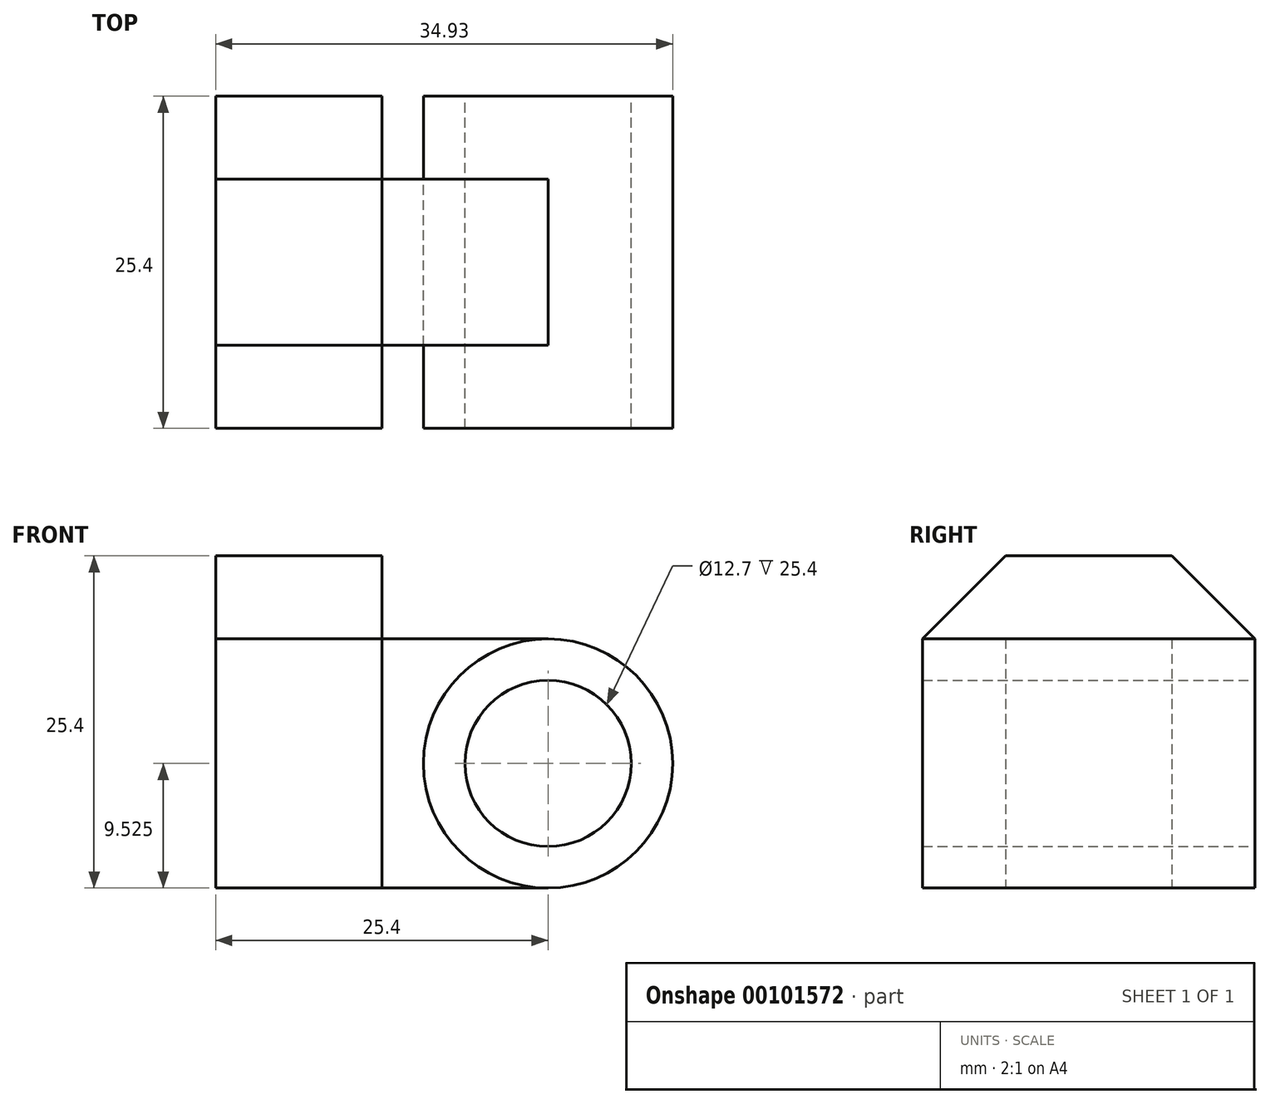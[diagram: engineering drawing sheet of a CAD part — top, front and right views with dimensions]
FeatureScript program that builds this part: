
annotation { "Feature Type Name" : "Feature", "Feature Type Description" : "" }
export const myFeature = defineFeature(function(context is Context, id is Id, definition is map)
    precondition{}
    {
        {
            var Q0;
            Q0=qCreatedBy(makeId("Right.planeOp"),FACE);
            var sketch = newSketch(context, id + "F0", { "sketchPlane" : qUnion([Q0])});
            skLineSegment(sketch, "E0", {"start": v(0, 0) * mm, "end": v(-12.7, 0) * mm});
            skLineSegment(sketch, "E1", {"start": v(12.7, 0) * mm, "end": v(0, 0) * mm});
            skLineSegment(sketch, "E2", {"start": v(-12.7, 0) * mm, "end": v(-12.7, 19.05) * mm});
            skLineSegment(sketch, "E3", {"start": v(-12.7, 19.05) * mm, "end": v(-6.35, 25.4) * mm});
            skLineSegment(sketch, "E4", {"start": v(-6.35, 25.4) * mm, "end": v(6.35, 25.4) * mm});
            skLineSegment(sketch, "E5", {"start": v(6.35, 25.4) * mm, "end": v(12.7, 19.05) * mm});
            skLineSegment(sketch, "E6", {"start": v(12.7, 19.05) * mm, "end": v(12.7, 0) * mm});
            skLineSegment(sketch, "E7", {"start": v(0, 25.4) * mm, "end": v(0, 0) * mm, "construction": true});
            skLineSegment(sketch, "E8", {"start": v(-12.7, 0) * mm, "end": v(-12.7, 25.4) * mm, "construction": true});
            skLineSegment(sketch, "E9", {"start": v(-12.7, 25.4) * mm, "end": v(12.7, 25.4) * mm, "construction": true});
            skLineSegment(sketch, "E10", {"start": v(12.7, 25.4) * mm, "end": v(12.7, 0) * mm, "construction": true});
            skLineSegment(sketch, "E11", {"start": v(12.7, 0) * mm, "end": v(-12.7, 0) * mm, "construction": true});
            skSolve(sketch);
        }
        {
            var Q0;
            Q0 = qSketchRegion(id + "F0", true);
            extrude(context, id + "F1", {"entities" : qUnion([Q0]), "depth" : 12.7 * mm});
        }
        {
            var Q0;
            Q0=qCreatedBy(makeId("Front.planeOp"),FACE);
            var sketch = newSketch(context, id + "F2", { "sketchPlane" : qUnion([Q0])});
            skLineSegment(sketch, "E12", {"start": v(12.7, 0) * mm, "end": v(25.4, 0) * mm});
            skLineSegment(sketch, "E13", {"start": v(25.4, 19.05) * mm, "end": v(12.7, 19.05) * mm});
            skLineSegment(sketch, "E14", {"start": v(12.7, 19.05) * mm, "end": v(12.7, 0) * mm});
            skPoint(sketch, "E15", {"position": v(25.4, 9.53) * mm});
            skCircle(sketch, "E16", {"center": v(25.4, 9.53) * mm, "radius": 6.35 * mm});
            skCircle(sketch, "E17", {"center": v(25.4, 9.53) * mm, "radius": 9.53 * mm});
            skSolve(sketch);
        }
        {
            var Q0;
            Q0=makeQuery(id+"F2.imprint","IMPRINT",FACE,{"disambiguationData":[TD([[makeQuery(id+"F2.imprint","IMPRINT",EDGE,{"derivedFrom":sQuery(id+"F2.wireOp",EDGE,"E16")}),-1.0]])]});
            extrude(context, id + "F3", {"entities" : qUnion([Q0]), "endBound" : BoundingType.SYMMETRIC, "depth" : 25.4 * mm});
        }
        {
            var Q0;
            {var subQ0=sQuery(id+"F2.wireOp",EDGE,"E12");Q0=makeQuery(id+"F2.imprint","IMPRINT",FACE,{"disambiguationData":[TD([[makeQuery(id+"F2.imprint","IMPRINT",EDGE,{"derivedFrom":subQ0}),1.0]])]});}
            extrude(context, id + "F4", {"entities" : qUnion([Q0]), "endBound" : BoundingType.SYMMETRIC, "depth" : 12.7 * mm});
        }
    });
